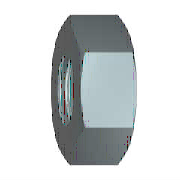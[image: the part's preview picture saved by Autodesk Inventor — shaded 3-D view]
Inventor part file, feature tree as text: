
AUTODESK INVENTOR PART (.ipt)
format: ipt  version: 2024.2 (Build 282272000, 272)  size: 172,032 bytes
history: native  units: mm (DEFAULTED — no unit token found)
features: chamfer x1, hole x1, other x1, plane x1
ambient origin geometry x7: Origin, YZ Plane, XZ Plane, X Axis, Y Axis, Z Axis, Center Point
bodies: Solid1 (feature_tree), Body (feature_tree)
feature tree (4):
  chamfer  "Chamfer1"  Distance=24.248711mm
  hole  "Thread"  [1 undecoded]
  other  "Work Axis1"
  plane  "Work Plane1"
note: 1 required parameter value undecoded (feature->parameter linkage not recoverable at this tier; creation-order binding heuristic only, values carry confidence <= 0.55)
